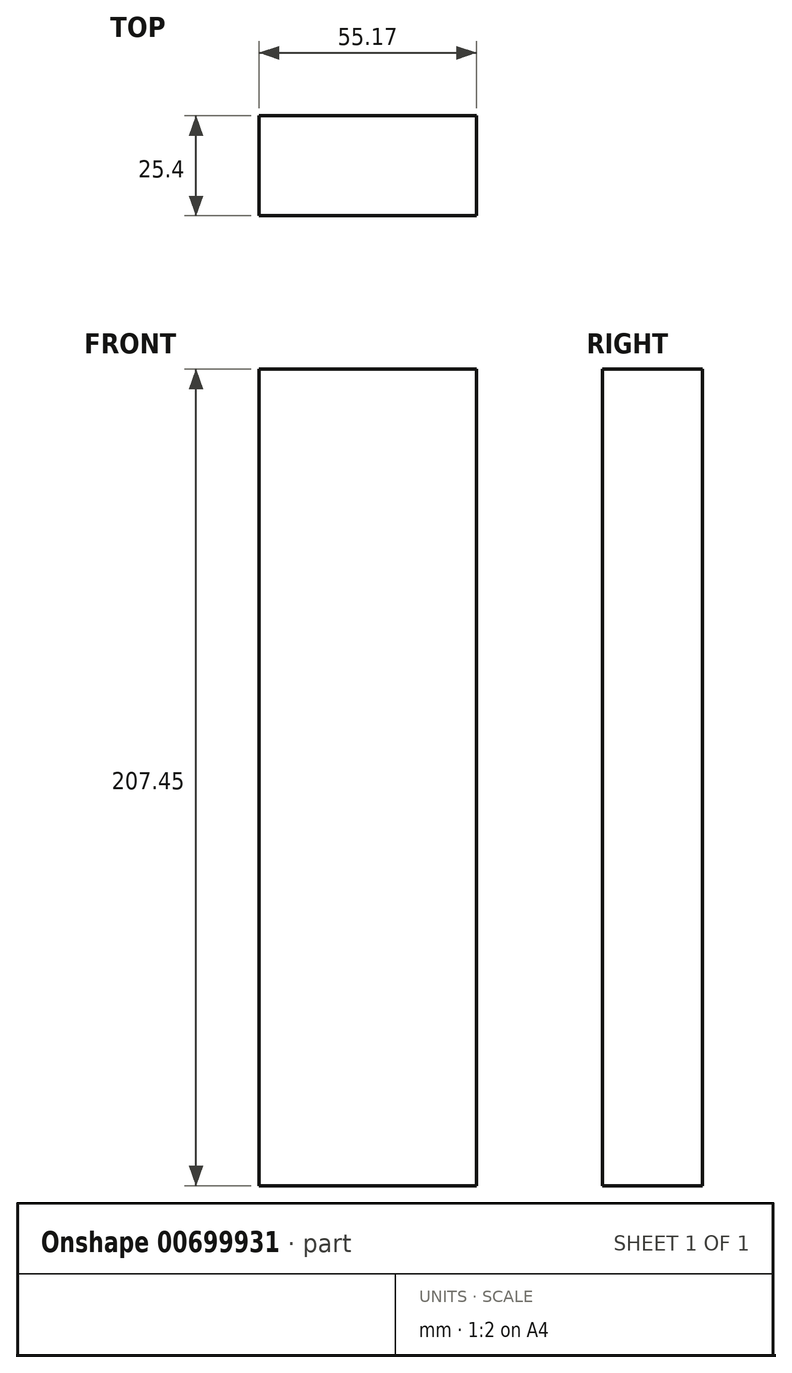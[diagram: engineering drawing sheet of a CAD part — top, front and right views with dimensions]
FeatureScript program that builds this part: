
annotation { "Feature Type Name" : "Feature", "Feature Type Description" : "" }
export const myFeature = defineFeature(function(context is Context, id is Id, definition is map)
    precondition{}
    {
        {
            var Q0;
            Q0=qCreatedBy(makeId("Front.planeOp"),FACE);
            var sketch = newSketch(context, id + "F0", { "sketchPlane" : qUnion([Q0])});
            skLineSegment(sketch, "E0.bottom", {"start": v(-67.15, 70.15) * mm, "end": v(-11.98, 70.15) * mm});
            skLineSegment(sketch, "E0.top", {"start": v(-67.15, -137.3) * mm, "end": v(-11.98, -137.3) * mm});
            skLineSegment(sketch, "E0.left", {"start": v(-67.15, 70.15) * mm, "end": v(-67.15, -137.3) * mm});
            skLineSegment(sketch, "E0.right", {"start": v(-11.98, 70.15) * mm, "end": v(-11.98, -137.3) * mm});
            skSolve(sketch);
        }
        {
            var Q0;
            Q0=makeQuery(id+"F0.imprint","IMPRINT",FACE,{"disambiguationData":[TD([[makeQuery(id+"F0.imprint","IMPRINT",EDGE,{"derivedFrom":sQuery(id+"F0.wireOp",EDGE,"E0.bottom")}),-1.0]])]});
            extrude(context, id + "F1", {"entities" : qUnion([Q0]), "depth" : 25.4 * mm, "offsetDistance" : 25.4 * mm});
        }
    });
